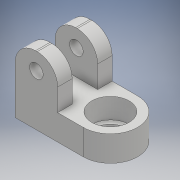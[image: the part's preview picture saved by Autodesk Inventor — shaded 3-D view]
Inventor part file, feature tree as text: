
AUTODESK INVENTOR PART (.ipt)
format: ipt  version: 2017 (Build 210142000, 142)  size: 153,088 bytes
history: native  units: mm
features: extrude x4, sketch x4, fillet x1
ambient origin geometry x8: Origin, YZ Plane, XZ Plane, XY Plane, X Axis, Y Axis, Z Axis, Center Point
bodies: Solid1 (feature_tree)
feature tree (9):
  extrude  "Extrusion1"  Depth=5.0mm
  extrude  "Extrusion2"  Depth=15.0mm TaperAngle=0.0deg
  extrude  "Extrusion3"  Depth=15.0mm
  fillet  "Fillet1"  Radius=25.0mm
  extrude  "Extrusion4"  Depth=10.0mm
  sketch  "Sketch1"  dims[d0=22.0mm d1=5.0mm]
  sketch  "Sketch2"  dims[d2=40.0mm d3=15.0mm d4=0.0mm]
  sketch  "Sketch3"  dims[d5=25.0mm d6=15.0mm d7=25.0mm d8=0.0mm]
  sketch  "Sketch4"  dims[d9=8.0mm d10=10.0mm d11=25.0mm d12=0.0mm d13=12.0mm d14=16.0mm d15=3.0mm d16=0.0mm]
